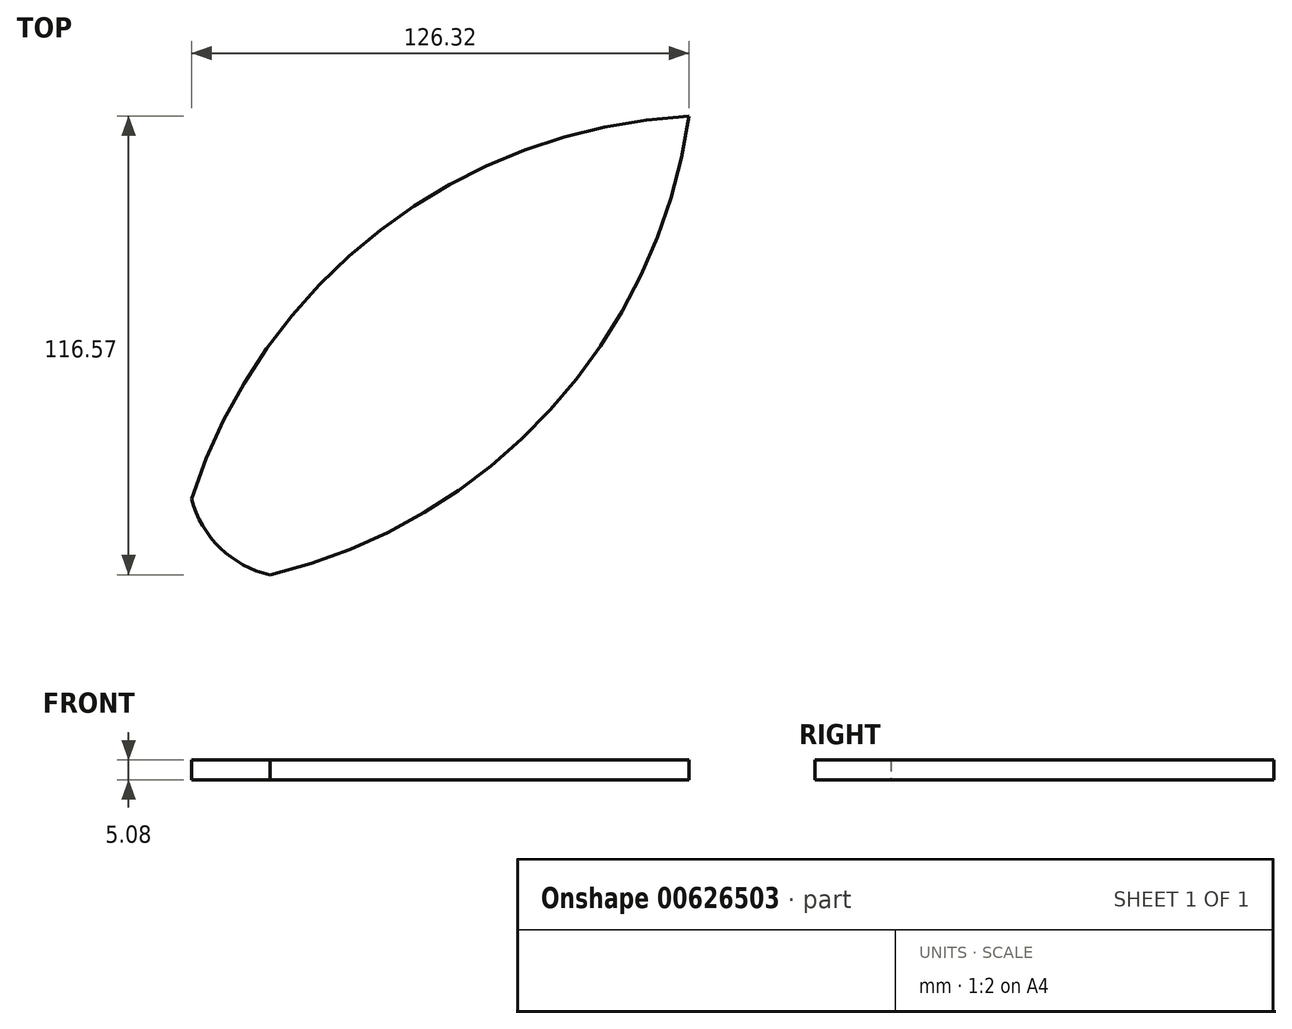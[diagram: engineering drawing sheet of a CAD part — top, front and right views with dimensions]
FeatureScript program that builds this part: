
annotation { "Feature Type Name" : "Feature", "Feature Type Description" : "" }
export const myFeature = defineFeature(function(context is Context, id is Id, definition is map)
    precondition{}
    {
        {
            var Q0;
            Q0=qCreatedBy(makeId("Top.planeOp"),FACE);
            var sketch = newSketch(context, id + "F0", { "sketchPlane" : qUnion([Q0])});
            skPoint(sketch, "E0.middle", {"position": v(0, 0) * mm});
            skArc(sketch, "E1", {"start": v(65.63, 59.94) * mm, "mid": v(-12.7, 31.01) * mm, "end": v(-60.69, -37.31) * mm});
            skArc(sketch, "E2.MirrorCS", {"start": v(65.63, 59.94) * mm, "mid": v(30.4, -14.74) * mm, "end": v(-40.76, -56.63) * mm});
            skPoint(sketch, "E0.left.start.orphan", {"position": v(65.63, -59.94) * mm});
            skPoint(sketch, "E0.top.end.orphan", {"position": v(-65.63, 59.94) * mm});
            skArc(sketch, "E3", {"start": v(-60.69, -37.31) * mm, "mid": v(-53.47, -49.8) * mm, "end": v(-40.76, -56.63) * mm});
            skPoint(sketch, "E4.start.orphan", {"position": v(-65.63, -59.94) * mm});
            skSolve(sketch);
        }
        {
            var Q0;
            Q0 = qSketchRegion(id + "F0", true);
            extrude(context, id + "F1", {"entities" : qUnion([Q0]), "depth" : 5.08 * mm, "offsetDistance" : 25.4 * mm});
        }
    });
